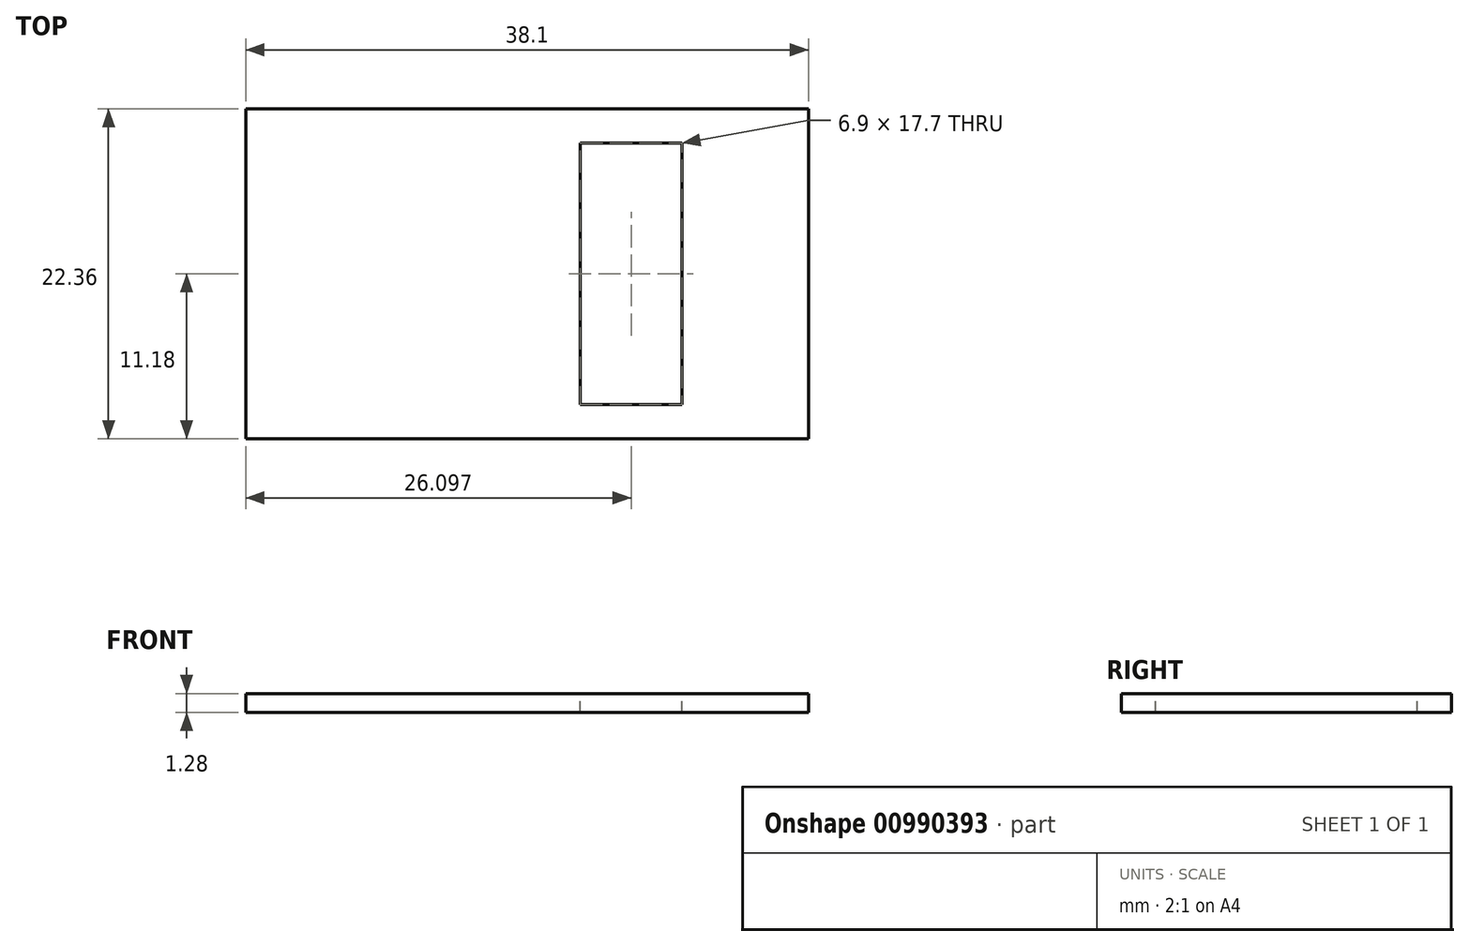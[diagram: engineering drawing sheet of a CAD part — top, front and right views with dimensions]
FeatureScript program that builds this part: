
annotation { "Feature Type Name" : "Feature", "Feature Type Description" : "" }
export const myFeature = defineFeature(function(context is Context, id is Id, definition is map)
    precondition{}
    {
        {
            var Q0;
            Q0=qCreatedBy(makeId("Right.planeOp"),FACE);
            var sketch = newSketch(context, id + "F0", { "sketchPlane" : qUnion([Q0])});
            skLineSegment(sketch, "E0.bottom", {"start": v(11.18, -0.63) * mm, "end": v(-11.18, -0.64) * mm});
            skLineSegment(sketch, "E0.top", {"start": v(11.18, 0.64) * mm, "end": v(-11.18, 0.63) * mm});
            skLineSegment(sketch, "E0.left", {"start": v(11.18, -0.63) * mm, "end": v(11.18, 0.64) * mm});
            skLineSegment(sketch, "E0.right", {"start": v(-11.18, -0.64) * mm, "end": v(-11.18, 0.63) * mm});
            skPoint(sketch, "E0.middle", {"position": v(0, 0) * mm});
            skSolve(sketch);
        }
        {
            var Q0;
            Q0=makeQuery(id+"F0.imprint","IMPRINT",FACE,{"disambiguationData":[TD([[makeQuery(id+"F0.imprint","IMPRINT",EDGE,{"derivedFrom":sQuery(id+"F0.wireOp",EDGE,"E0.bottom")}),-1.0]])]});
            extrude(context, id + "F1", {"entities" : qUnion([Q0]), "depth" : 38.1 * mm, "offsetDistance" : 25.4 * mm});
        }
        {
            var Q0;
            Q0=qCreatedBy(makeId("Top.planeOp"),FACE);
            var sketch = newSketch(context, id + "F2", { "sketchPlane" : qUnion([Q0])});
            skLineSegment(sketch, "E1.bottom", {"start": v(22.65, -8.85) * mm, "end": v(29.55, -8.85) * mm});
            skLineSegment(sketch, "E1.top", {"start": v(22.65, 8.85) * mm, "end": v(29.55, 8.85) * mm});
            skLineSegment(sketch, "E1.left", {"start": v(22.65, -8.85) * mm, "end": v(22.65, 8.85) * mm});
            skLineSegment(sketch, "E1.right", {"start": v(29.55, -8.85) * mm, "end": v(29.55, 8.85) * mm});
            skPoint(sketch, "E1.middle", {"position": v(26.1, 0) * mm});
            skSolve(sketch);
        }
        {
            var Q0;
            Q0 = qSketchRegion(id + "F2", true);
            var Q1;
            Q1=makeQuery(id+"F2.imprint","IMPRINT",FACE,{"disambiguationData":[TD([[makeQuery(id+"F2.imprint","IMPRINT",EDGE,{"derivedFrom":sQuery(id+"F2.wireOp",EDGE,"E1.bottom")}),1.0]])]});
            extrude(context, id + "F3", {"entities" : qUnion([Q0, Q1]), "operationType" : NewBodyOperationType.REMOVE, "oppositeDirection" : true, "depth" : 25.4 * mm, "offsetDistance" : 25.4 * mm, "hasSecondDirection" : true, "secondDirectionOppositeDirection" : false, "secondDirectionDepth" : 25.4 * mm});
        }
    });
